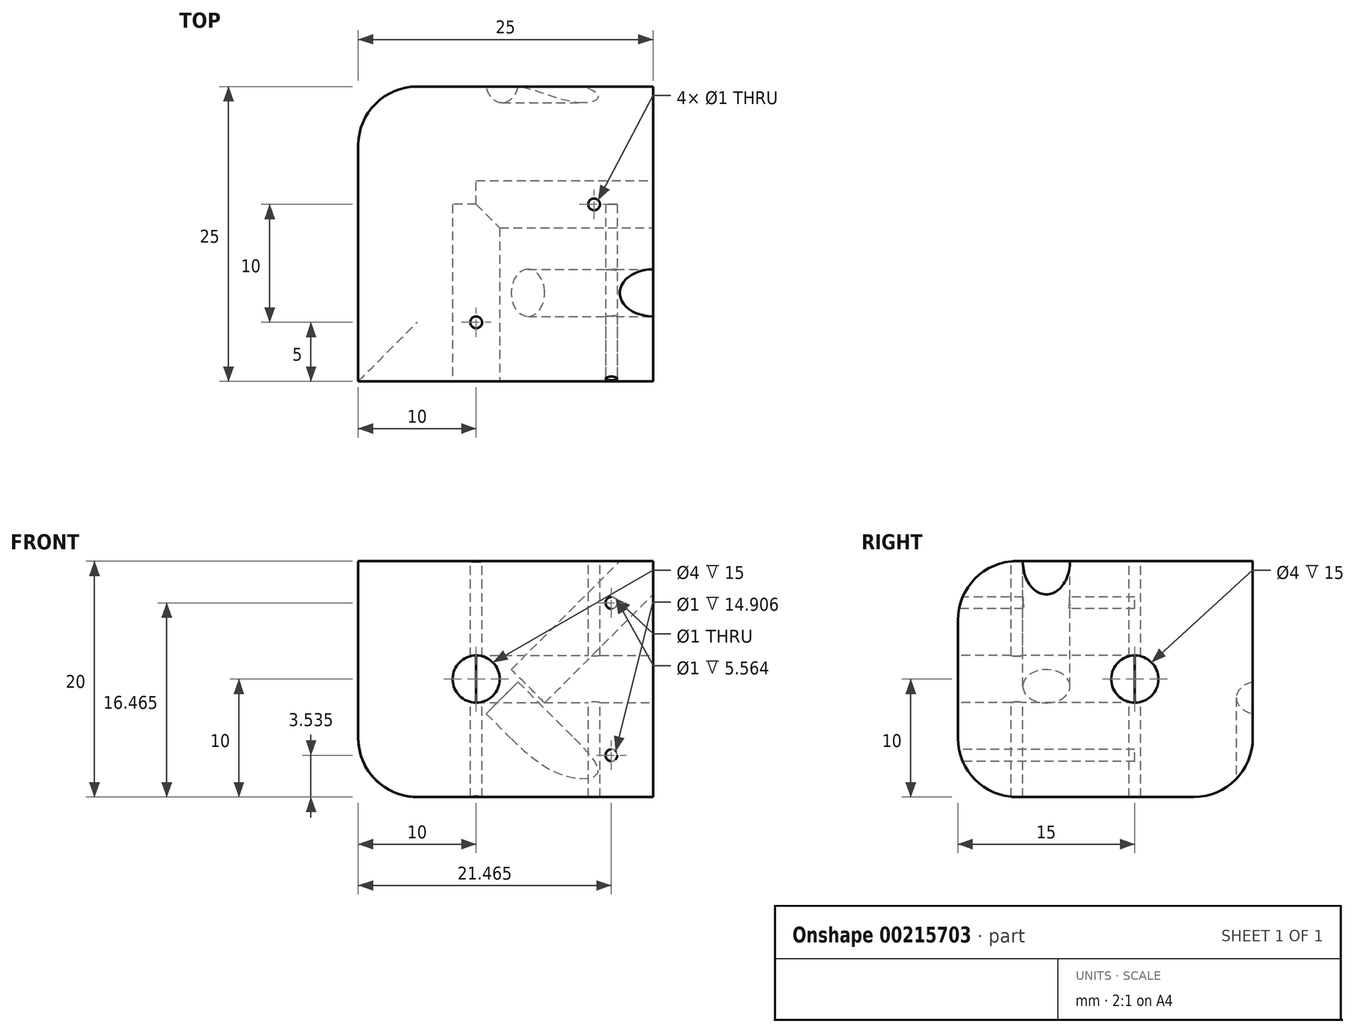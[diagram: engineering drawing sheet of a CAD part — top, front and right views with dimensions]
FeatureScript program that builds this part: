
annotation { "Feature Type Name" : "Feature", "Feature Type Description" : "" }
export const myFeature = defineFeature(function(context is Context, id is Id, definition is map)
    precondition{}
    {
        {
            var Q0;
            Q0=qCreatedBy(makeId("Top.planeOp"),FACE);
            var sketch = newSketch(context, id + "F0", { "sketchPlane" : qUnion([Q0])});
            skLineSegment(sketch, "E0.bottom", {"start": v(-15, 15) * mm, "end": v(15, 15) * mm});
            skLineSegment(sketch, "E0.top", {"start": v(-15, -15) * mm, "end": v(15, -15) * mm});
            skLineSegment(sketch, "E0.left", {"start": v(-15, 15) * mm, "end": v(-15, -15) * mm});
            skLineSegment(sketch, "E0.right", {"start": v(15, 15) * mm, "end": v(15, -15) * mm});
            skSolve(sketch);
        }
        {
            var Q0;
            Q0 = qSketchRegion(id + "F0", true);
            extrude(context, id + "F1", {"entities" : qUnion([Q0]), "depth" : 20 * mm});
        }
        {
            var Q0;
            Q0=makeQuery(id+"F1.opExtrude","SWEPT_FACE",FACE,{"disambiguationData":[OSD([sQuery(id+"F0.wireOp",EDGE,"E0.right")])]});
            var sketch = newSketch(context, id + "F2", { "sketchPlane" : qUnion([Q0])});
            skCircle(sketch, "E1", {"center": v(0, 10) * mm, "radius": 2 * mm});
            skPoint(sketch, "E1.centerSnap0", {"position": v(-15, 10) * mm});
            skSolve(sketch);
        }
        {
            var Q0;
            Q0 = qSketchRegion(id + "F2", true);
            extrude(context, id + "F3", {"entities" : qUnion([Q0]), "operationType" : NewBodyOperationType.REMOVE, "oppositeDirection" : true, "depth" : 15 * mm});
        }
        {
            var Q0;
            Q0=makeQuery(id+"F1.opExtrude","SWEPT_FACE",FACE,{"disambiguationData":[OSD([sQuery(id+"F0.wireOp",EDGE,"E0.top")])]});
            var sketch = newSketch(context, id + "F4", { "sketchPlane" : qUnion([Q0])});
            skCircle(sketch, "E2", {"center": v(0, 10) * mm, "radius": 2 * mm});
            skPoint(sketch, "E2.centerSnap0", {"position": v(15, 10) * mm});
            skLineSegment(sketch, "E3", {"start": v(15, 20) * mm, "end": v(5, 10) * mm, "construction": true});
            skLineSegment(sketch, "E4", {"start": v(5, 10) * mm, "end": v(15, 0) * mm, "construction": true});
            skCircle(sketch, "E5", {"center": v(11.46, 16.46) * mm, "radius": 0.5 * mm});
            skCircle(sketch, "E6", {"center": v(11.46, 3.54) * mm, "radius": 0.5 * mm});
            skSolve(sketch);
        }
        {
            var Q0;
            Q0 = qSketchRegion(id + "F4", true);
            extrude(context, id + "F5", {"entities" : qUnion([Q0]), "operationType" : NewBodyOperationType.REMOVE, "oppositeDirection" : true, "depth" : 15 * mm});
        }
        {
            var Q0;
            Q0=makeQuery(id+"F1.opExtrude","CAP_EDGE",EDGE,{"disambiguationData":[OSD([sQuery(id+"F0.wireOp",EDGE,"E0.right")])],"isStart":false});
            cPlane(context, id + "F6", {"entities" : qUnion([Q0]), "cplaneType" : CPlaneType.LINE_ANGLE, "offset" : 25 * mm, "angle" : 135 * degree, "width" : 150 * mm, "height" : 150 * mm});
        }
        {
            var Q0;
            Q0=qCreatedBy(id+"F6.planeOp",FACE);
            var sketch = newSketch(context, id + "F7", { "sketchPlane" : qUnion([Q0])});
            skCircle(sketch, "E7", {"center": v(-7.5, 3.54) * mm, "radius": 2 * mm});
            skSolve(sketch);
        }
        {
            var Q0;
            Q0 = qSketchRegion(id + "F7", true);
            extrude(context, id + "F8", {"entities" : qUnion([Q0]), "operationType" : NewBodyOperationType.REMOVE, "oppositeDirection" : true, "depth" : 15 * mm});
        }
        {
            var Q0;
            Q0=makeQuery(id+"F1.opExtrude","CAP_EDGE",EDGE,{"disambiguationData":[OSD([sQuery(id+"F0.wireOp",EDGE,"E0.right")])],"isStart":true});
            cPlane(context, id + "F9", {"entities" : qUnion([Q0]), "cplaneType" : CPlaneType.LINE_ANGLE, "offset" : 25 * mm, "angle" : 45 * degree, "width" : 150 * mm, "height" : 150 * mm});
        }
        {
            var Q0;
            Q0=qCreatedBy(id+"F9.planeOp",FACE);
            var sketch = newSketch(context, id + "F10", { "sketchPlane" : qUnion([Q0])});
            skCircle(sketch, "E8", {"center": v(10.6, 7.5) * mm, "radius": 2 * mm});
            skSolve(sketch);
        }
        {
            var Q0;
            Q0 = qSketchRegion(id + "F10", true);
            extrude(context, id + "F11", {"entities" : qUnion([Q0]), "operationType" : NewBodyOperationType.REMOVE, "oppositeDirection" : true, "depth" : 15 * mm});
        }
        {
            var Q0;
            Q0=makeQuery(id+"F1.opExtrude","CAP_FACE",FACE,{"disambiguationData":[OSD([sQuery(id+"F0.wireOp",EDGE,"E0.bottom"),sQuery(id+"F0.wireOp",EDGE,"E0.top"),sQuery(id+"F0.wireOp",EDGE,"E0.left"),sQuery(id+"F0.wireOp",EDGE,"E0.right")])],"isStart":false});
            var sketch = newSketch(context, id + "F12", { "sketchPlane" : qUnion([Q0])});
            skLineSegment(sketch, "E9", {"start": v(-10, -15) * mm, "end": v(-60, -15) * mm});
            skLineSegment(sketch, "E10", {"start": v(-60, -15) * mm, "end": v(-60, 50) * mm});
            skLineSegment(sketch, "E11", {"start": v(-60, 50) * mm, "end": v(15, 50) * mm});
            skLineSegment(sketch, "E12", {"start": v(15, 50) * mm, "end": v(15, 10) * mm});
            skLineSegment(sketch, "E13", {"start": v(15, 10) * mm, "end": v(-10, 10) * mm});
            skLineSegment(sketch, "E14", {"start": v(-10, 10) * mm, "end": v(-10, -15) * mm});
            skCircle(sketch, "E15", {"center": v(10, 0) * mm, "radius": 0.5 * mm});
            skCircle(sketch, "E16", {"center": v(0, -10) * mm, "radius": 0.5 * mm});
            skSolve(sketch);
        }
        {
            var Q0;
            Q0 = qSketchRegion(id + "F12", true);
            extrude(context, id + "F13", {"entities" : qUnion([Q0]), "operationType" : NewBodyOperationType.REMOVE, "endBound" : BoundingType.THROUGH_ALL, "oppositeDirection" : true, "depth" : 25 * mm});
        }
        {
            var Q0;
            Q0=makeQuery(id+"F13.boolean.opBoolean","COPY",EDGE,{"derivedFrom":makeQuery(id+"F13.opExtrude","SWEPT_EDGE",EDGE,{"disambiguationData":[OSD([sQuery(id+"F0.wireOp",EDGE,"E0.top"),sQuery(id+"F12.wireOp",EDGE,"E9"),sQuery(id+"F12.wireOp",EDGE,"E14")])]})});
            var Q1;
            Q1=makeQuery(id+"F1.opExtrude","CAP_EDGE",EDGE,{"disambiguationData":[OSD([sQuery(id+"F0.wireOp",EDGE,"E0.top")])],"isStart":false});
            var Q2;
            Q2=makeQuery(id+"F13.boolean.opBoolean","COPY",EDGE,{"derivedFrom":makeQuery(id+"F13.opExtrude","CAP_EDGE",EDGE,{"disambiguationData":[OSD([sQuery(id+"F12.wireOp",EDGE,"E14")])],"isStart":true})});
            var Q3;
            Q3=makeQuery(id+"F13.boolean.opBoolean","COPY",EDGE,{"derivedFrom":makeQuery(id+"F13.opExtrude","CAP_EDGE",EDGE,{"disambiguationData":[OSD([sQuery(id+"F12.wireOp",EDGE,"E13")])],"isStart":true})});
            var Q4;
            Q4=makeQuery(id+"F13.boolean.opBoolean","COPY",EDGE,{"derivedFrom":makeQuery(id+"F13.opExtrude","SWEPT_EDGE",EDGE,{"disambiguationData":[OSD([sQuery(id+"F12.wireOp",EDGE,"E13"),sQuery(id+"F12.wireOp",EDGE,"E14")])]})});
            var Q5;
            Q5=makeQuery(id+"F13.boolean.opBoolean","INTERSECT",EDGE,{"derivedFrom":[makeQuery(id+"F1.opExtrude","CAP_FACE",FACE,{"disambiguationData":[OSD([sQuery(id+"F0.wireOp",EDGE,"E0.bottom"),sQuery(id+"F0.wireOp",EDGE,"E0.top"),sQuery(id+"F0.wireOp",EDGE,"E0.left"),sQuery(id+"F0.wireOp",EDGE,"E0.right")])],"isStart":true}),makeQuery(id+"F13.opExtrude","SWEPT_FACE",FACE,{"disambiguationData":[OSD([sQuery(id+"F12.wireOp",EDGE,"E13")])]})]});
            var Q6;
            Q6=makeQuery(id+"F1.opExtrude","CAP_EDGE",EDGE,{"disambiguationData":[OSD([sQuery(id+"F0.wireOp",EDGE,"E0.top")])],"isStart":true});
            var Q7;
            Q7=makeQuery(id+"F13.boolean.opBoolean","INTERSECT",EDGE,{"derivedFrom":[makeQuery(id+"F1.opExtrude","CAP_FACE",FACE,{"disambiguationData":[OSD([sQuery(id+"F0.wireOp",EDGE,"E0.bottom"),sQuery(id+"F0.wireOp",EDGE,"E0.top"),sQuery(id+"F0.wireOp",EDGE,"E0.left"),sQuery(id+"F0.wireOp",EDGE,"E0.right")])],"isStart":true}),makeQuery(id+"F13.opExtrude","SWEPT_FACE",FACE,{"disambiguationData":[OSD([sQuery(id+"F12.wireOp",EDGE,"E14")])]})]});
            fillet(context, id + "F14", {"entities" : qUnion([Q0, Q1, Q2, Q3, Q4, Q5, Q6, Q7]), "radius" : 5 * mm, "tangentPropagation" : true, "allowEdgeOverflow" : false});
        }
    });
